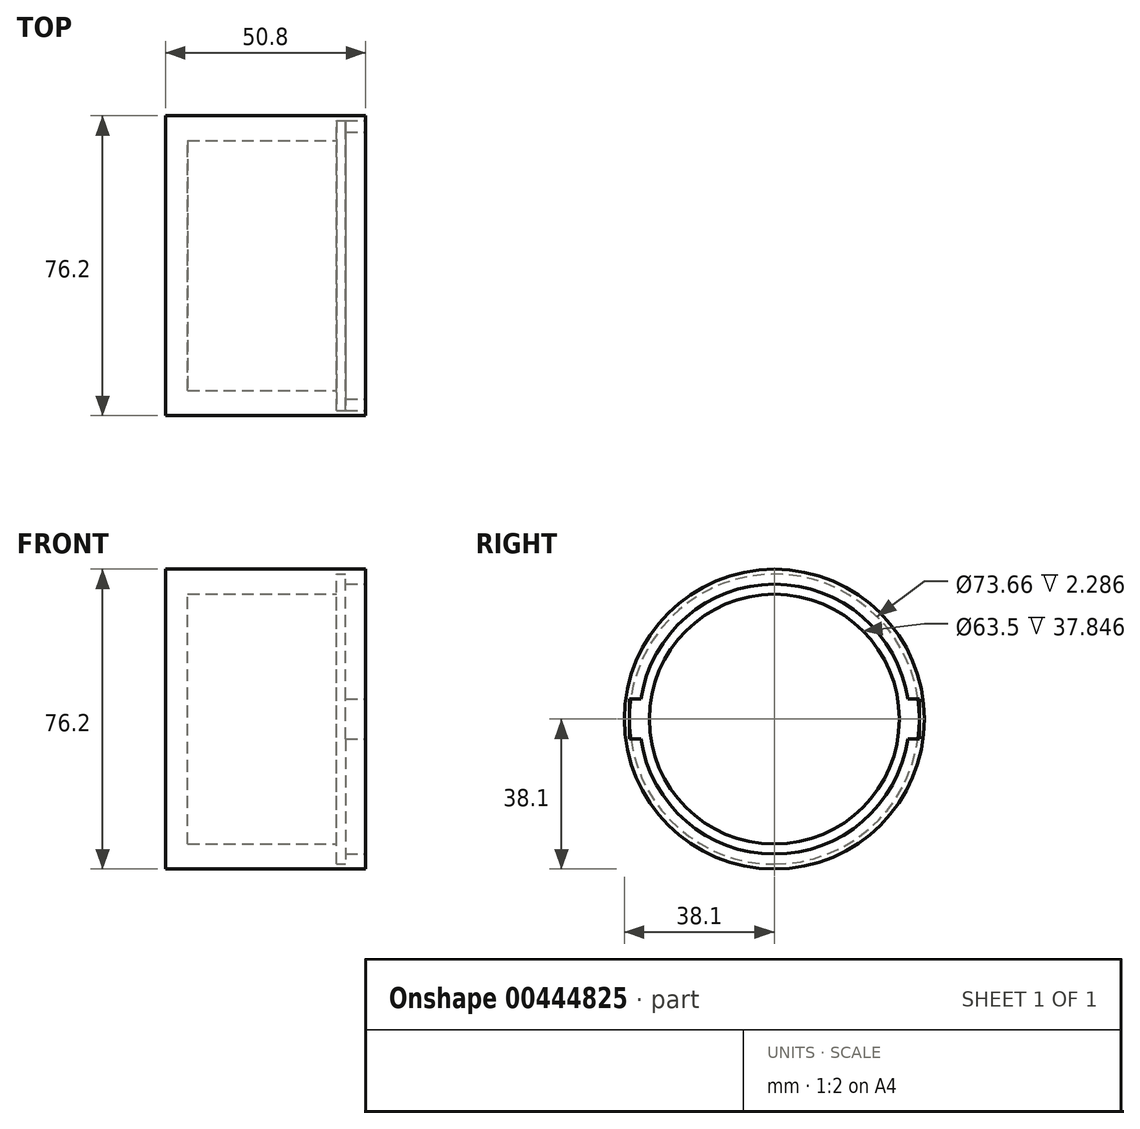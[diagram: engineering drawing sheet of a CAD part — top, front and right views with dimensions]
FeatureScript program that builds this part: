
annotation { "Feature Type Name" : "Feature", "Feature Type Description" : "" }
export const myFeature = defineFeature(function(context is Context, id is Id, definition is map)
    precondition{}
    {
        {
            var Q0;
            Q0=qCreatedBy(makeId("Right.planeOp"),FACE);
            var sketch = newSketch(context, id + "F0", { "sketchPlane" : qUnion([Q0])});
            skCircle(sketch, "E0", {"center": v(0, 0) * mm, "radius": 38.1 * mm});
            skSolve(sketch);
        }
        {
            var Q0;
            Q0=makeQuery(id+"F0.imprint","IMPRINT",FACE,{"disambiguationData":[TD([[makeQuery(id+"F0.imprint","IMPRINT",EDGE,{"derivedFrom":sQuery(id+"F0.wireOp",EDGE,"E0")}),1.0]])]});
            extrude(context, id + "F1", {"entities" : qUnion([Q0]), "depth" : 50.8 * mm});
        }
        {
            var Q0;
            Q0=makeQuery(id+"F1.opExtrude","CAP_FACE",FACE,{"disambiguationData":[OSD([sQuery(id+"F0.wireOp",EDGE,"E0")])],"isStart":false});
            var sketch = newSketch(context, id + "F2", { "sketchPlane" : qUnion([Q0])});
            skCircle(sketch, "E1", {"center": v(0, 0) * mm, "radius": 31.75 * mm});
            skSolve(sketch);
        }
        {
            var Q0;
            Q0 = qSketchRegion(id + "F2", true);
            extrude(context, id + "F3", {"entities" : qUnion([Q0]), "operationType" : NewBodyOperationType.REMOVE, "oppositeDirection" : true, "depth" : 45.2 * mm});
        }
        {
            var Q0;
            Q0=makeQuery(id+"F1.opExtrude","CAP_FACE",FACE,{"disambiguationData":[OSD([sQuery(id+"F0.wireOp",EDGE,"E0")])],"isStart":false});
            var sketch = newSketch(context, id + "F4", { "sketchPlane" : qUnion([Q0])});
            skCircle(sketch, "E2", {"center": v(0, 0) * mm, "radius": 34.3 * mm});
            skSolve(sketch);
        }
        {
            var Q0;
            Q0 = qSketchRegion(id + "F4", true);
            extrude(context, id + "F5", {"entities" : qUnion([Q0]), "operationType" : NewBodyOperationType.REMOVE, "oppositeDirection" : true, "depth" : 5.08 * mm});
        }
        {
            var Q0;
            Q0=makeQuery(id+"F1.opExtrude","CAP_FACE",FACE,{"disambiguationData":[OSD([sQuery(id+"F0.wireOp",EDGE,"E0")])],"isStart":false});
            var sketch = newSketch(context, id + "F6", { "sketchPlane" : qUnion([Q0])});
            skLineSegment(sketch, "E3.bottom", {"start": v(-36.83, -5.08) * mm, "end": v(36.83, -5.08) * mm});
            skLineSegment(sketch, "E3.top", {"start": v(-36.83, 5.08) * mm, "end": v(36.83, 5.08) * mm});
            skLineSegment(sketch, "E3.left", {"start": v(-36.83, -5.08) * mm, "end": v(-36.83, 5.08) * mm});
            skLineSegment(sketch, "E3.right", {"start": v(36.83, -5.08) * mm, "end": v(36.83, 5.08) * mm});
            skPoint(sketch, "E3.middle", {"position": v(0, 0) * mm});
            skSolve(sketch);
        }
        {
            var Q0;
            Q0 = qSketchRegion(id + "F6", true);
            extrude(context, id + "F7", {"entities" : qUnion([Q0]), "operationType" : NewBodyOperationType.REMOVE, "oppositeDirection" : true, "depth" : 5.08 * mm});
        }
        {
            var Q0;
            Q0=makeQuery(id+"F7.boolean.opBoolean","MERGE",FACE,{"derivedFrom":[makeQuery(id+"F5.boolean.opBoolean","COPY",FACE,{"derivedFrom":makeQuery(id+"F5.opExtrude","CAP_FACE",FACE,{"disambiguationData":[OSD([sQuery(id+"F4.wireOp",EDGE,"E2")])],"isStart":false})}),makeQuery(id+"F7.opExtrude","CAP_FACE",FACE,{"disambiguationData":[OSD([sQuery(id+"F6.wireOp",EDGE,"E3.bottom"),sQuery(id+"F6.wireOp",EDGE,"E3.top"),sQuery(id+"F6.wireOp",EDGE,"E3.left"),sQuery(id+"F6.wireOp",EDGE,"E3.right")])],"isStart":false})]});
            var sketch = newSketch(context, id + "F8", { "sketchPlane" : qUnion([Q0])});
            skCircle(sketch, "E4", {"center": v(0, 0) * mm, "radius": 36.83 * mm});
            skSolve(sketch);
        }
        {
            var Q0;
            Q0 = qSketchRegion(id + "F8", true);
            extrude(context, id + "F9", {"entities" : qUnion([Q0]), "operationType" : NewBodyOperationType.REMOVE, "oppositeDirection" : true, "depth" : 2.3 * mm});
        }
    });
